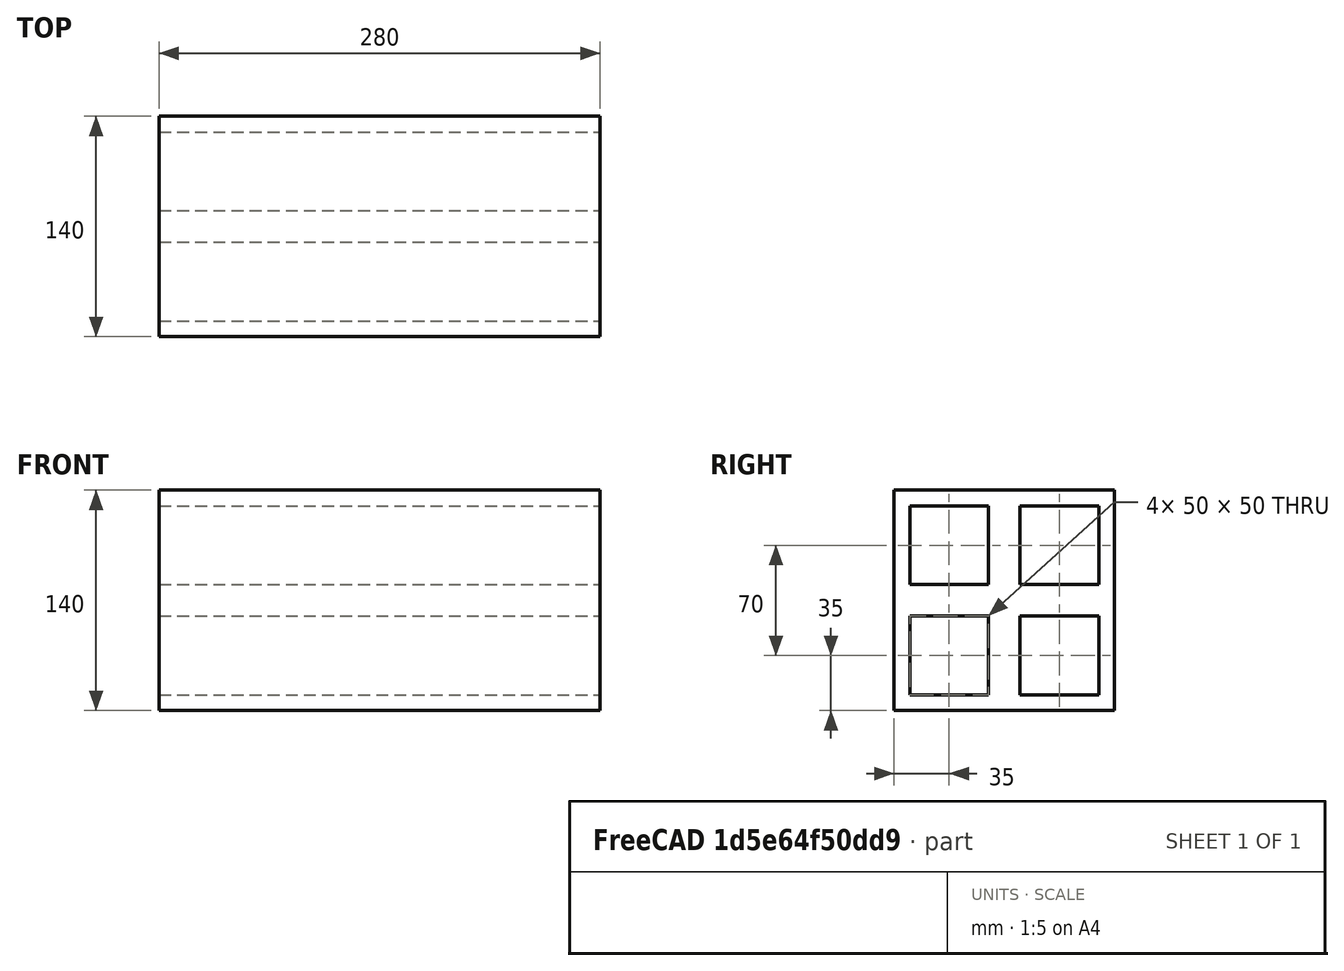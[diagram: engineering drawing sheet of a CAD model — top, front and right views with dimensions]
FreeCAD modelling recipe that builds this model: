
FCSTD DOCUMENT  (FreeCAD 0.21R33694 (Git))
Label: OJT1_T19R01.quadrat4
License: All rights reserved
LicenseURL: http://en.wikipedia.org/wiki/All_rights_reserved
objects: Sketcher::SketchObject×1, PartDesign::Pad×1, PartDesign::Body×1
note: 4 computed .brp shape members not serialized (recipe doc carries the construction recipe); baked Part::Feature solids carry a one-line shape summary decoded from their .brp

FEATURE [Sketcher::SketchObject] Sketch
  FullyConstrained = true
  MapMode = 5
  Placement = pos=(0,0,0) rot=(0.57735,0.57735,0.57735;2.0944rad)
  Support = -> [YZ_Plane]
  sketch-geometry (20):
    g0: LineSegment StartX=10 StartY=60 StartZ=0 EndX=60 EndY=60 EndZ=0
    g1: LineSegment StartX=60 StartY=60 StartZ=0 EndX=60 EndY=10 EndZ=0
    g2: LineSegment StartX=60 StartY=10 StartZ=0 EndX=10 EndY=10 EndZ=0
    g3: LineSegment StartX=10 StartY=10 StartZ=0 EndX=10 EndY=60 EndZ=0
    g4: LineSegment StartX=-10 StartY=60 StartZ=0 EndX=-60 EndY=60 EndZ=0
    g5: LineSegment StartX=-60 StartY=60 StartZ=0 EndX=-60 EndY=10 EndZ=0
    g6: LineSegment StartX=-60 StartY=10 StartZ=0 EndX=-10 EndY=10 EndZ=0
    g7: LineSegment StartX=-10 StartY=10 StartZ=0 EndX=-10 EndY=60 EndZ=0
    g8: LineSegment StartX=-10 StartY=-10 StartZ=0 EndX=-60 EndY=-10 EndZ=0
    g9: LineSegment StartX=-60 StartY=-10 StartZ=0 EndX=-60 EndY=-60 EndZ=0
    g10: LineSegment StartX=-60 StartY=-60 StartZ=0 EndX=-10 EndY=-60 EndZ=0
    g11: LineSegment StartX=-10 StartY=-60 StartZ=0 EndX=-10 EndY=-10 EndZ=0
    g12: LineSegment StartX=10 StartY=-10 StartZ=0 EndX=60 EndY=-10 EndZ=0
    g13: LineSegment StartX=60 StartY=-10 StartZ=0 EndX=60 EndY=-60 EndZ=0
    g14: LineSegment StartX=60 StartY=-60 StartZ=0 EndX=10 EndY=-60 EndZ=0
    g15: LineSegment StartX=10 StartY=-60 StartZ=0 EndX=10 EndY=-10 EndZ=0
    g16: LineSegment StartX=-70 StartY=70 StartZ=0 EndX=70 EndY=70 EndZ=0
    g17: LineSegment StartX=70 StartY=70 StartZ=0 EndX=70 EndY=-70 EndZ=0
    g18: LineSegment StartX=70 StartY=-70 StartZ=0 EndX=-70 EndY=-70 EndZ=0
    g19: LineSegment StartX=-70 StartY=-70 StartZ=0 EndX=-70 EndY=70 EndZ=0
  constraints (55):
    c: Coincident(g0,g1)
    c: Coincident(g1,g2)
    c: Coincident(g2,g3)
    c: Coincident(g3,g0)
    c: Horizontal(g0)
    c: Horizontal(g2)
    c: Vertical(g1)
    c: Vertical(g3)
    c: Coincident(g4,g5)
    c: Coincident(g5,g6)
    c: Coincident(g6,g7)
    c: Coincident(g7,g4)
    c: Horizontal(g4)
    c: Horizontal(g6)
    c: Vertical(g5)
    c: Vertical(g7)
    c: Coincident(g8,g9)
    c: Coincident(g9,g10)
    c: Coincident(g10,g11)
    c: Coincident(g11,g8)
    c: Horizontal(g8)
    c: Horizontal(g10)
    c: Vertical(g9)
    c: Vertical(g11)
    c: Coincident(g12,g13)
    c: Coincident(g13,g14)
    c: Coincident(g14,g15)
    c: Coincident(g15,g12)
    c: Horizontal(g12)
    c: Horizontal(g14)
    c: Vertical(g13)
    c: Vertical(g15)
    c: Coincident(g16,g17)
    c: Coincident(g17,g18)
    c: Coincident(g18,g19)
    c: Coincident(g19,g16)
    c: Horizontal(g18)
    c: Vertical(g17)
    c: DistanceY(g19,g19) = 140
    c: DistanceX(g4,g4) = 50
    c: Distance(g8,g6) = 20
    c: Equal(g5,g4)
    c: Equal(g9,g10)
    c: Equal(g13,g14)
    c: Equal(g2,g1)
    c: Equal(g7,g3)
    c: Equal(g12,g2)
    c: Equal(g15,g11)
    c: Symmetric(g5,g8,g-1)
    c: Symmetric(g8,g12,g-2)
    c: Distance(g14,g10) = 20
    c: Symmetric(g2,g12,g-1)
    c: Symmetric(g16,g18,g-1)
    c: Equal(g16,g19)
    c: Symmetric(g16,g16,g-2)
FEATURE [PartDesign::Pad] Pad
  Direction = (1,-2e-16,3e-16)
  Length = 280
  Length2 = 10
  Placement = pos=(0,0,0) rot=(1,1,1;2.0944rad)
  Profile = -> Sketch
  ReferenceAxis = -> Sketch [N_Axis]
  Refine = true
  Type = 0
FEATURE [PartDesign::Body] Body  label="Cos"
  Group = -> [Sketch,Pad]
  Origin = -> Origin
  Tip = -> Pad
